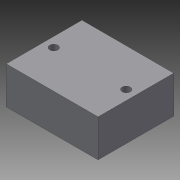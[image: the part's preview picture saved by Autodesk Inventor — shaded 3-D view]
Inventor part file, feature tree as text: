
AUTODESK INVENTOR PART (.ipt)
format: ipt  version: 2015 (Build 190159000, 159)  size: 79,872 bytes
history: native  units: mm
features: extrude x2, sketch x2
ambient origin geometry x8: Origin, YZ Plane, XZ Plane, XY Plane, X Axis, Y Axis, Z Axis, Center Point
bodies: Solid1 (feature_tree)
feature tree (4):
  extrude  "Extrusion1"  Depth=30.5mm
  extrude  "Extrusion2"  Depth=15.0mm
  sketch  "Sketch1"  dims[d0=37.0mm d1=30.5mm]
  sketch  "Sketch2"  dims[d2=15.0mm d3=0.0mm d4=3.3mm d5=3.3mm d6=29.21mm d7=15.0mm d8=0.0mm]
